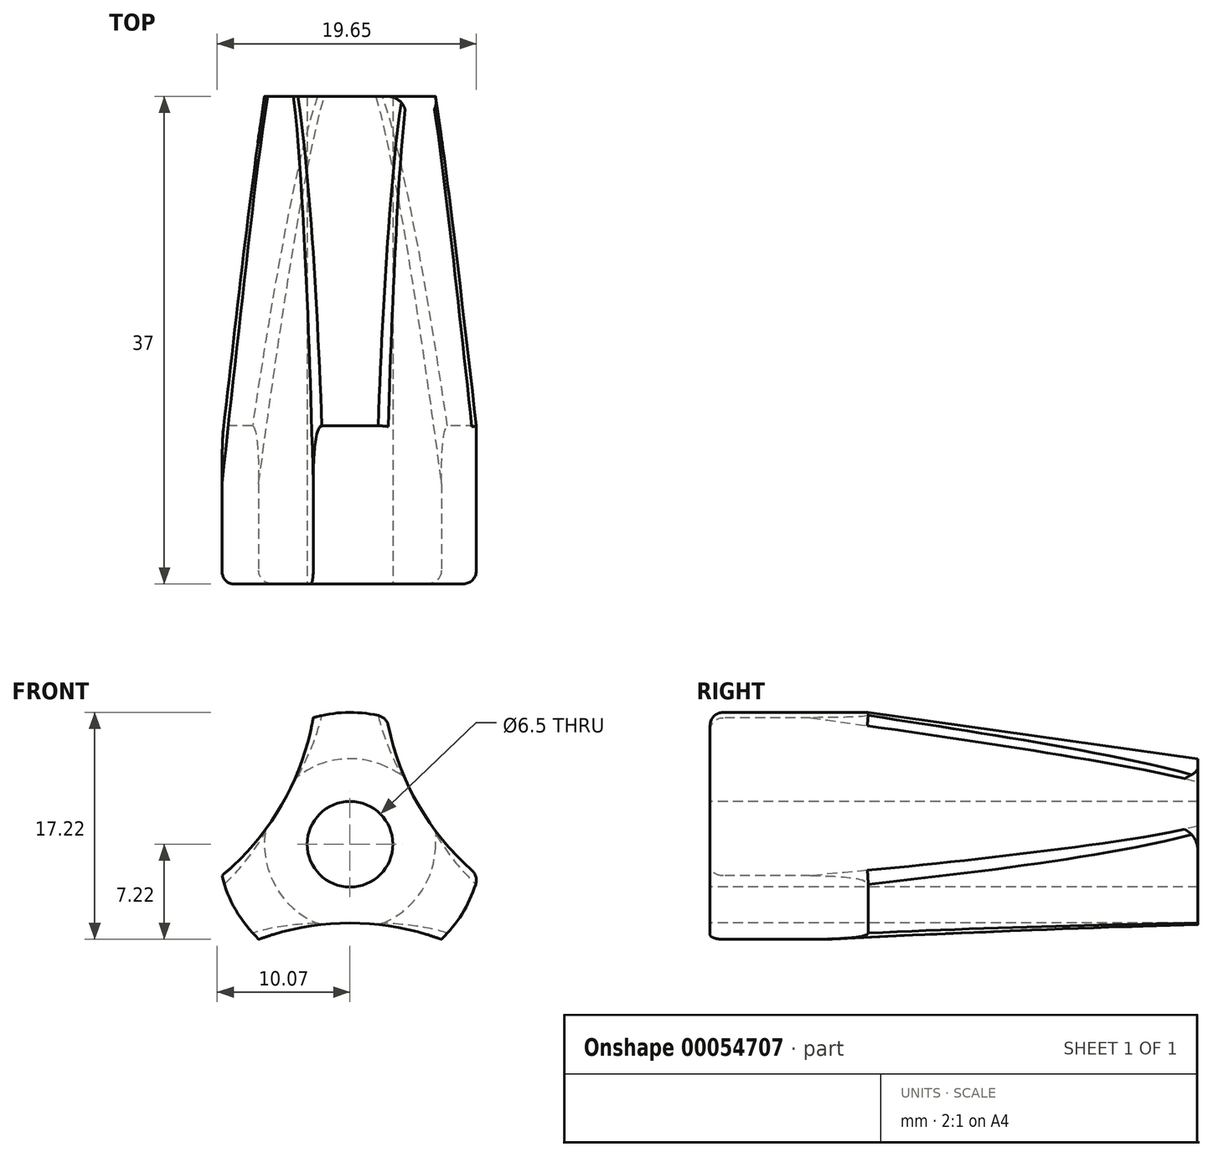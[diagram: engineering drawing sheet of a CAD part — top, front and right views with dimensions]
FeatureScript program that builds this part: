
annotation { "Feature Type Name" : "Feature", "Feature Type Description" : "" }
export const myFeature = defineFeature(function(context is Context, id is Id, definition is map)
    precondition{}
    {
        {
            var Q0;
            Q0=qCreatedBy(makeId("Front.planeOp"),FACE);
            var sketch = newSketch(context, id + "F0", { "sketchPlane" : qUnion([Q0])});
            skCircle(sketch, "E0", {"center": v(0, 0) * mm, "radius": 10 * mm});
            skSolve(sketch);
        }
        {
            var Q0;
            Q0=makeQuery(id+"F0.imprint","IMPRINT",FACE,{"disambiguationData":[TD([[makeQuery(id+"F0.imprint","IMPRINT",EDGE,{"derivedFrom":sQuery(id+"F0.wireOp",EDGE,"E0")}),1.0]])]});
            extrude(context, id + "F1", {"entities" : qUnion([Q0]), "oppositeDirection" : true, "depth" : 12 * mm});
        }
        {
            var Q0;
            Q0=makeQuery(id+"F1.opExtrude","CAP_FACE",FACE,{"disambiguationData":[OSD([sQuery(id+"F0.wireOp",EDGE,"E0")])],"isStart":false});
            var sketch = newSketch(context, id + "F2", { "sketchPlane" : qUnion([Q0])});
            skSolve(sketch);
        }
        {
            var Q0;
            Q0=makeQuery(id+"F2.imprint","IMPRINT",FACE,{"disambiguationData":[TD([[makeQuery(id+"F2.imprint","IMPRINT",EDGE,{"derivedFrom":makeQuery(id+"F1.opExtrude","CAP_EDGE",EDGE,{"disambiguationData":[OSD([sQuery(id+"F0.wireOp",EDGE,"E0")])],"isStart":false})}),-1.0]])]});
            var sketch = newSketch(context, id + "F3", { "sketchPlane" : qUnion([Q0])});
            skCircle(sketch, "E1", {"center": v(0, 0) * mm, "radius": 10 * mm});
            skSolve(sketch);
        }
        {
            var Q0;
            Q0 = qSketchRegion(id + "F3", true);
            extrude(context, id + "F4", {"entities" : qUnion([Q0]), "operationType" : NewBodyOperationType.ADD, "depth" : 25 * mm, "hasDraft" : true, "draftAngle" : 8 * degree, "draftPullDirection" : true});
        }
        {
            var Q0;
            Q0=makeQuery(id+"F1.opExtrude","CAP_FACE",FACE,{"disambiguationData":[OSD([sQuery(id+"F0.wireOp",EDGE,"E0")])],"isStart":true});
            var sketch = newSketch(context, id + "F5", { "sketchPlane" : qUnion([Q0])});
            skCircle(sketch, "E2", {"center": v(0, 0) * mm, "radius": 3.25 * mm});
            skSolve(sketch);
        }
        {
            var Q0;
            Q0=makeQuery(id+"F5.imprint","IMPRINT",FACE,{"disambiguationData":[TD([[makeQuery(id+"F5.imprint","IMPRINT",EDGE,{"derivedFrom":sQuery(id+"F5.wireOp",EDGE,"E2")}),1.0]])]});
            extrude(context, id + "F6", {"entities" : qUnion([Q0]), "operationType" : NewBodyOperationType.REMOVE, "oppositeDirection" : true, "depth" : 39.3 * mm});
        }
        {
            var Q0;
            Q0=makeQuery(id+"F1.opExtrude","CAP_FACE",FACE,{"disambiguationData":[OSD([sQuery(id+"F0.wireOp",EDGE,"E0")])],"isStart":true});
            var sketch = newSketch(context, id + "F7", { "sketchPlane" : qUnion([Q0])});
            skCircle(sketch, "E3.cCircle", {"center": v(0, 0) * mm, "radius": 25.98 * mm, "construction": true});
            skLineSegment(sketch, "E3.0", {"start": v(0, -25.98) * mm, "end": v(-22.5, 13) * mm});
            skLineSegment(sketch, "E3.1", {"start": v(-22.5, 13) * mm, "end": v(22.5, 13) * mm});
            skLineSegment(sketch, "E3.2", {"start": v(22.5, 13) * mm, "end": v(0, -25.98) * mm});
            skCircle(sketch, "E4", {"center": v(22.5, 13) * mm, "radius": 20 * mm});
            skCircle(sketch, "E5", {"center": v(-22.5, 13) * mm, "radius": 20 * mm});
            skCircle(sketch, "E6", {"center": v(0, -25.98) * mm, "radius": 20 * mm});
            skSolve(sketch);
        }
        {
            var Q0;
            {var subQ0=sQuery(id+"F7.wireOp",EDGE,"E5");var subQ1=makeQuery(id+"F1.opExtrude","CAP_EDGE",EDGE,{"disambiguationData":[OSD([sQuery(id+"F0.wireOp",EDGE,"E0")])],"isStart":true});var subQ2=makeQuery(id+"F7.imprint","INTERSECT",VERTEX,{"disambiguationData":[OD(0.0)],"derivedFrom":[subQ1,subQ0]});Q0=makeQuery(id+"F7.imprint","IMPRINT",FACE,{"disambiguationData":[TD([[makeQuery(id+"F7.imprint","IMPRINT",EDGE,{"disambiguationData":[TD([[subQ2,-1.0]])],"derivedFrom":subQ0}),1.0]])]});}
            var Q1;
            {var subQ0=sQuery(id+"F7.wireOp",EDGE,"E4");var subQ1=makeQuery(id+"F1.opExtrude","CAP_EDGE",EDGE,{"disambiguationData":[OSD([sQuery(id+"F0.wireOp",EDGE,"E0")])],"isStart":true});var subQ2=makeQuery(id+"F7.imprint","INTERSECT",VERTEX,{"disambiguationData":[OD(0.0)],"derivedFrom":[subQ1,subQ0]});Q1=makeQuery(id+"F7.imprint","IMPRINT",FACE,{"disambiguationData":[TD([[makeQuery(id+"F7.imprint","IMPRINT",EDGE,{"disambiguationData":[TD([[subQ2,-1.0]])],"derivedFrom":subQ0}),1.0]])]});}
            var Q2;
            {var subQ0=sQuery(id+"F7.wireOp",EDGE,"E6");var subQ1=makeQuery(id+"F1.opExtrude","CAP_EDGE",EDGE,{"disambiguationData":[OSD([sQuery(id+"F0.wireOp",EDGE,"E0")])],"isStart":true});var subQ2=makeQuery(id+"F7.imprint","INTERSECT",VERTEX,{"disambiguationData":[OD(0.0)],"derivedFrom":[subQ1,subQ0]});Q2=makeQuery(id+"F7.imprint","IMPRINT",FACE,{"disambiguationData":[TD([[makeQuery(id+"F7.imprint","IMPRINT",EDGE,{"disambiguationData":[TD([[subQ2,-1.0]])],"derivedFrom":subQ0}),1.0]])]});}
            extrude(context, id + "F8", {"entities" : qUnion([Q0, Q1, Q2]), "operationType" : NewBodyOperationType.REMOVE, "oppositeDirection" : true, "depth" : 50 * mm});
        }
        {
            var Q0;
            {var subQ0=sQuery(id+"F7.wireOp",EDGE,"E5");var subQ1=sQuery(id+"F0.wireOp",EDGE,"E0");Q0=makeQuery(id+"F8.boolean.opBoolean","COPY",EDGE,{"derivedFrom":makeQuery(id+"F8.opExtrude","SWEPT_EDGE",EDGE,{"disambiguationData":[OSD([subQ1,subQ0]),TDD([makeQuery(id+"F7.imprint","INTERSECT",VERTEX,{"disambiguationData":[OD(1.0)],"derivedFrom":[makeQuery(id+"F1.opExtrude","CAP_EDGE",EDGE,{"disambiguationData":[OSD([subQ1])],"isStart":true}),subQ0]})])]})});}
            var Q1;
            Q1=makeQuery(id+"F8.boolean.opBoolean","INTERSECT",EDGE,{"disambiguationData":[OD(1.0)],"derivedFrom":[makeQuery(id+"F4.opExtrude","SWEPT_FACE",FACE,{"disambiguationData":[OSD([sQuery(id+"F3.wireOp",EDGE,"E1")])]}),makeQuery(id+"F8.opExtrude","SWEPT_FACE",FACE,{"disambiguationData":[OSD([sQuery(id+"F7.wireOp",EDGE,"E5")])]})]});
            var Q2;
            Q2=makeQuery(id+"F8.boolean.opBoolean","COPY",EDGE,{"derivedFrom":makeQuery(id+"F8.opExtrude","CAP_EDGE",EDGE,{"disambiguationData":[OSD([sQuery(id+"F7.wireOp",EDGE,"E5")])],"isStart":true})});
            var Q3;
            {var subQ0=sQuery(id+"F7.wireOp",EDGE,"E5");var subQ1=sQuery(id+"F0.wireOp",EDGE,"E0");Q3=makeQuery(id+"F8.boolean.opBoolean","COPY",EDGE,{"derivedFrom":makeQuery(id+"F8.opExtrude","SWEPT_EDGE",EDGE,{"disambiguationData":[OSD([subQ1,subQ0]),TDD([makeQuery(id+"F7.imprint","INTERSECT",VERTEX,{"disambiguationData":[OD(0.0)],"derivedFrom":[makeQuery(id+"F1.opExtrude","CAP_EDGE",EDGE,{"disambiguationData":[OSD([subQ1])],"isStart":true}),subQ0]})])]})});}
            var Q4;
            Q4=makeQuery(id+"F8.boolean.opBoolean","INTERSECT",EDGE,{"disambiguationData":[OD(0.0)],"derivedFrom":[makeQuery(id+"F4.opExtrude","SWEPT_FACE",FACE,{"disambiguationData":[OSD([sQuery(id+"F3.wireOp",EDGE,"E1")])]}),makeQuery(id+"F8.opExtrude","SWEPT_FACE",FACE,{"disambiguationData":[OSD([sQuery(id+"F7.wireOp",EDGE,"E5")])]})]});
            var Q5;
            {var subQ0=sQuery(id+"F0.wireOp",EDGE,"E0");Q5=makeQuery(id+"F8.boolean.opBoolean","SPLIT",EDGE,{"disambiguationData":[TD([makeQuery(id+"F1.opExtrude","SWEPT_FACE",FACE,{"disambiguationData":[OSD([subQ0])]}),makeQuery(id+"F1.opExtrude","CAP_FACE",FACE,{"disambiguationData":[OSD([subQ0])],"isStart":true}),makeQuery(id+"F8.opExtrude","SWEPT_FACE",FACE,{"disambiguationData":[OSD([sQuery(id+"F7.wireOp",EDGE,"E5")])]}),makeQuery(id+"F8.opExtrude","SWEPT_FACE",FACE,{"disambiguationData":[OSD([sQuery(id+"F7.wireOp",EDGE,"E6")])]})])],"derivedFrom":makeQuery(id+"F1.opExtrude","CAP_EDGE",EDGE,{"disambiguationData":[OSD([subQ0])],"isStart":true})});}
            var Q6;
            {var subQ0=sQuery(id+"F7.wireOp",EDGE,"E6");var subQ1=sQuery(id+"F0.wireOp",EDGE,"E0");Q6=makeQuery(id+"F8.boolean.opBoolean","COPY",EDGE,{"derivedFrom":makeQuery(id+"F8.opExtrude","SWEPT_EDGE",EDGE,{"disambiguationData":[OSD([subQ1,subQ0]),TDD([makeQuery(id+"F7.imprint","INTERSECT",VERTEX,{"disambiguationData":[OD(1.0)],"derivedFrom":[makeQuery(id+"F1.opExtrude","CAP_EDGE",EDGE,{"disambiguationData":[OSD([subQ1])],"isStart":true}),subQ0]})])]})});}
            var Q7;
            Q7=makeQuery(id+"F8.boolean.opBoolean","INTERSECT",EDGE,{"disambiguationData":[OD(1.0)],"derivedFrom":[makeQuery(id+"F4.opExtrude","SWEPT_FACE",FACE,{"disambiguationData":[OSD([sQuery(id+"F3.wireOp",EDGE,"E1")])]}),makeQuery(id+"F8.opExtrude","SWEPT_FACE",FACE,{"disambiguationData":[OSD([sQuery(id+"F7.wireOp",EDGE,"E6")])]})]});
            var Q8;
            Q8=makeQuery(id+"F8.boolean.opBoolean","COPY",EDGE,{"derivedFrom":makeQuery(id+"F8.opExtrude","CAP_EDGE",EDGE,{"disambiguationData":[OSD([sQuery(id+"F7.wireOp",EDGE,"E6")])],"isStart":true})});
            var Q9;
            {var subQ0=sQuery(id+"F7.wireOp",EDGE,"E6");var subQ1=sQuery(id+"F0.wireOp",EDGE,"E0");Q9=makeQuery(id+"F8.boolean.opBoolean","COPY",EDGE,{"derivedFrom":makeQuery(id+"F8.opExtrude","SWEPT_EDGE",EDGE,{"disambiguationData":[OSD([subQ1,subQ0]),TDD([makeQuery(id+"F7.imprint","INTERSECT",VERTEX,{"disambiguationData":[OD(0.0)],"derivedFrom":[makeQuery(id+"F1.opExtrude","CAP_EDGE",EDGE,{"disambiguationData":[OSD([subQ1])],"isStart":true}),subQ0]})])]})});}
            var Q10;
            Q10=makeQuery(id+"F8.boolean.opBoolean","INTERSECT",EDGE,{"disambiguationData":[OD(0.0)],"derivedFrom":[makeQuery(id+"F4.opExtrude","SWEPT_FACE",FACE,{"disambiguationData":[OSD([sQuery(id+"F3.wireOp",EDGE,"E1")])]}),makeQuery(id+"F8.opExtrude","SWEPT_FACE",FACE,{"disambiguationData":[OSD([sQuery(id+"F7.wireOp",EDGE,"E6")])]})]});
            var Q11;
            Q11=makeQuery(id+"F8.boolean.opBoolean","COPY",FACE,{"derivedFrom":makeQuery(id+"F8.opExtrude","SWEPT_FACE",FACE,{"disambiguationData":[OSD([sQuery(id+"F7.wireOp",EDGE,"E4")])]})});
            var Q12;
            {var subQ0=sQuery(id+"F7.wireOp",EDGE,"E4");var subQ1=sQuery(id+"F0.wireOp",EDGE,"E0");Q12=makeQuery(id+"F8.boolean.opBoolean","COPY",EDGE,{"derivedFrom":makeQuery(id+"F8.opExtrude","SWEPT_EDGE",EDGE,{"disambiguationData":[OSD([subQ1,subQ0]),TDD([makeQuery(id+"F7.imprint","INTERSECT",VERTEX,{"disambiguationData":[OD(1.0)],"derivedFrom":[makeQuery(id+"F1.opExtrude","CAP_EDGE",EDGE,{"disambiguationData":[OSD([subQ1])],"isStart":true}),subQ0]})])]})});}
            var Q13;
            {var subQ0=sQuery(id+"F0.wireOp",EDGE,"E0");Q13=makeQuery(id+"F8.boolean.opBoolean","SPLIT",EDGE,{"disambiguationData":[TD([makeQuery(id+"F1.opExtrude","SWEPT_FACE",FACE,{"disambiguationData":[OSD([subQ0])]}),makeQuery(id+"F1.opExtrude","CAP_FACE",FACE,{"disambiguationData":[OSD([subQ0])],"isStart":true}),makeQuery(id+"F8.opExtrude","SWEPT_FACE",FACE,{"disambiguationData":[OSD([sQuery(id+"F7.wireOp",EDGE,"E4")])]}),makeQuery(id+"F8.opExtrude","SWEPT_FACE",FACE,{"disambiguationData":[OSD([sQuery(id+"F7.wireOp",EDGE,"E5")])]})])],"derivedFrom":makeQuery(id+"F1.opExtrude","CAP_EDGE",EDGE,{"disambiguationData":[OSD([subQ0])],"isStart":true})});}
            var Q14;
            {var subQ0=sQuery(id+"F0.wireOp",EDGE,"E0");Q14=makeQuery(id+"F8.boolean.opBoolean","SPLIT",EDGE,{"disambiguationData":[TD([makeQuery(id+"F1.opExtrude","SWEPT_FACE",FACE,{"disambiguationData":[OSD([subQ0])]}),makeQuery(id+"F1.opExtrude","CAP_FACE",FACE,{"disambiguationData":[OSD([subQ0])],"isStart":true}),makeQuery(id+"F8.opExtrude","SWEPT_FACE",FACE,{"disambiguationData":[OSD([sQuery(id+"F7.wireOp",EDGE,"E4")])]}),makeQuery(id+"F8.opExtrude","SWEPT_FACE",FACE,{"disambiguationData":[OSD([sQuery(id+"F7.wireOp",EDGE,"E6")])]})])],"derivedFrom":makeQuery(id+"F1.opExtrude","CAP_EDGE",EDGE,{"disambiguationData":[OSD([subQ0])],"isStart":true})});}
            fillet(context, id + "F9", {"entities" : qUnion([Q0, Q1, Q2, Q3, Q4, Q5, Q6, Q7, Q8, Q9, Q10, Q11, Q12, Q13, Q14]), "radius" : 1 * mm, "tangentPropagation" : true, "allowEdgeOverflow" : false});
        }
    });
